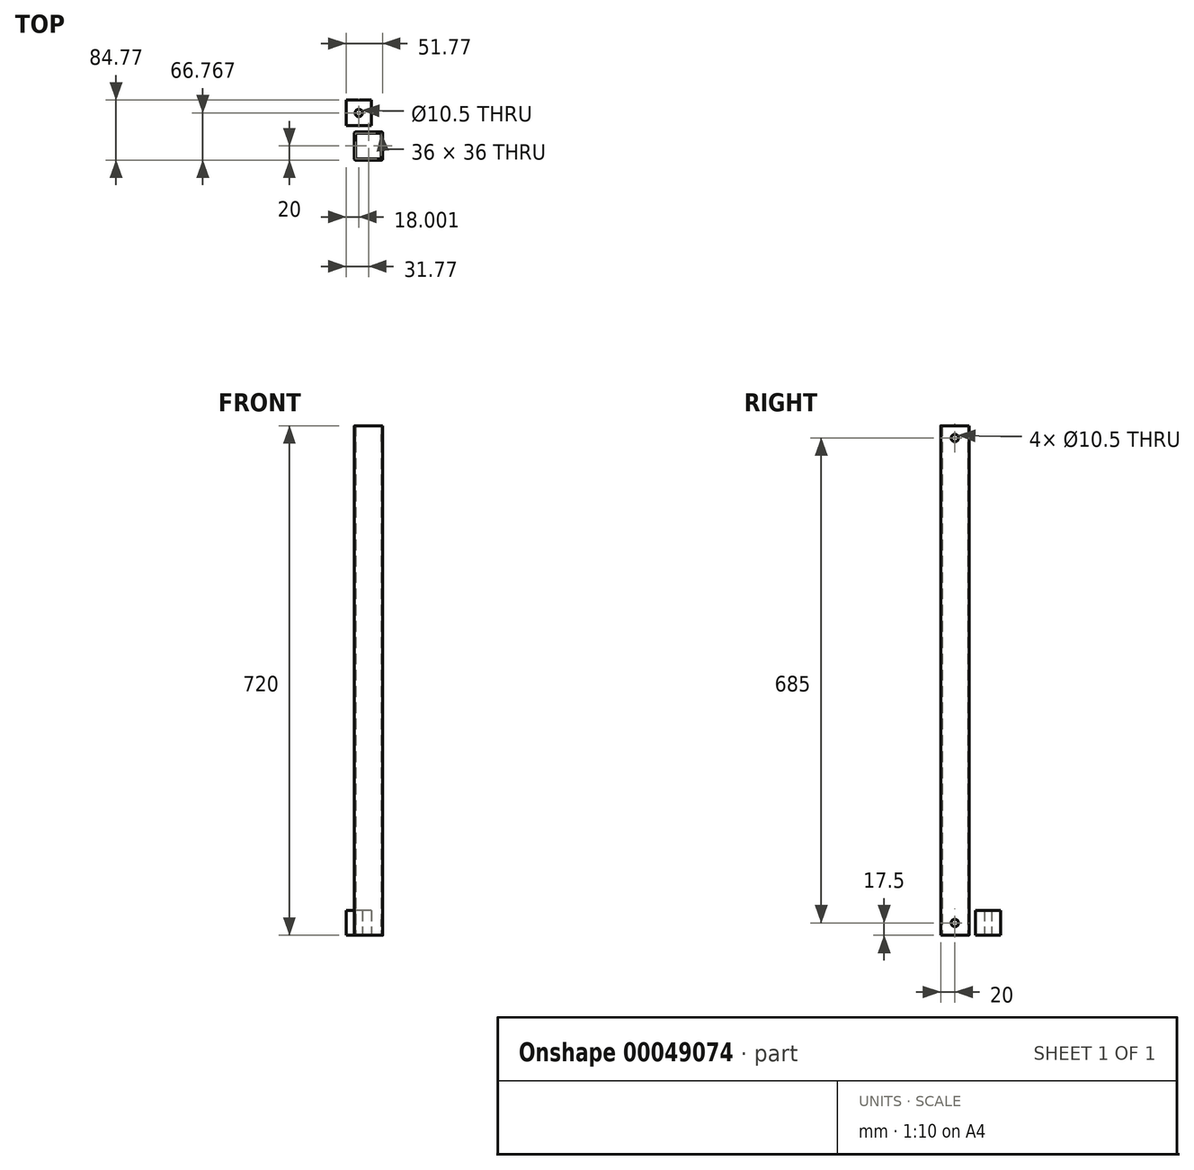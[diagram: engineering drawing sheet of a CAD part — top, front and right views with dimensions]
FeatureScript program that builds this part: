
annotation { "Feature Type Name" : "Feature", "Feature Type Description" : "" }
export const myFeature = defineFeature(function(context is Context, id is Id, definition is map)
    precondition{}
    {
        {
            var Q0;
            Q0=qCreatedBy(makeId("Top.planeOp"),FACE);
            var sketch = newSketch(context, id + "F0", { "sketchPlane" : qUnion([Q0])});
            skLineSegment(sketch, "E0.bottom", {"start": v(0, 0) * mm, "end": v(-40, 0) * mm});
            skLineSegment(sketch, "E0.top", {"start": v(0, -40) * mm, "end": v(-40, -40) * mm});
            skLineSegment(sketch, "E0.left", {"start": v(0, 0) * mm, "end": v(0, -40) * mm});
            skLineSegment(sketch, "E0.right", {"start": v(-40, 0) * mm, "end": v(-40, -40) * mm});
            skLineSegment(sketch, "E1.0", {"start": v(-2, -2) * mm, "end": v(-38, -2) * mm});
            skLineSegment(sketch, "E1.1", {"start": v(-2, -2) * mm, "end": v(-2, -38) * mm});
            skLineSegment(sketch, "E1.2", {"start": v(-2, -38) * mm, "end": v(-38, -38) * mm});
            skLineSegment(sketch, "E1.3", {"start": v(-38, -2) * mm, "end": v(-38, -38) * mm});
            skSolve(sketch);
        }
        {
            var Q0;
            Q0=qSketchRegion(id+"F0",true);
            extrude(context, id + "F1", {"entities" : qUnion([Q0]), "depth" : 720 * mm});
        }
        {
            var Q0;
            Q0=qCreatedBy(makeId("Top.planeOp"),FACE);
            var sketch = newSketch(context, id + "F2", { "sketchPlane" : qUnion([Q0])});
            skLineSegment(sketch, "E2.bottom", {"start": v(-15.77, 8.77) * mm, "end": v(-51.77, 8.77) * mm});
            skLineSegment(sketch, "E2.top", {"start": v(-15.77, 44.77) * mm, "end": v(-51.77, 44.77) * mm});
            skLineSegment(sketch, "E2.left", {"start": v(-15.77, 8.77) * mm, "end": v(-15.77, 44.77) * mm});
            skLineSegment(sketch, "E2.right", {"start": v(-51.77, 8.77) * mm, "end": v(-51.77, 44.77) * mm});
            skCircle(sketch, "E3", {"center": v(-33.77, 26.77) * mm, "radius": 5.25 * mm});
            skPoint(sketch, "E3.centerSnap0", {"position": v(-51.77, 26.77) * mm});
            skPoint(sketch, "E3.centerSnap1", {"position": v(-33.77, 8.77) * mm});
            skSolve(sketch);
        }
        {
            var Q0;
            Q0=qSketchRegion(id+"F2",true);
            extrude(context, id + "F3", {"entities" : qUnion([Q0]), "depth" : 35 * mm});
        }
        {
            var Q0;
            Q0=makeQuery(id+"F1.opExtrude","SWEPT_FACE",FACE,{"disambiguationData":[OSD([sQuery(id+"F0.wireOp",EDGE,"E0.right")])]});
            var sketch = newSketch(context, id + "F4", { "sketchPlane" : qUnion([Q0])});
            skLineSegment(sketch, "E4", {"start": v(40, 0) * mm, "end": v(0, 0) * mm});
            skLineSegment(sketch, "E5", {"start": v(40, 17.5) * mm, "end": v(0, 17.5) * mm});
            skCircle(sketch, "E6", {"center": v(20, 17.5) * mm, "radius": 5.25 * mm});
            skSolve(sketch);
        }
        {
            var Q0;
            Q0=sQuery(id+"F4.wireOp",VERTEX,"E6.center");
            var Q1;
            Q1=makeQuery(id+"F1.opExtrude","SWEPT_BODY",BODY,{"disambiguationData":[OSD([sQuery(id+"F0.wireOp",EDGE,"E0.bottom"),sQuery(id+"F0.wireOp",EDGE,"E0.top"),sQuery(id+"F0.wireOp",EDGE,"E0.left"),sQuery(id+"F0.wireOp",EDGE,"E0.right"),sQuery(id+"F0.wireOp",EDGE,"E1.0"),sQuery(id+"F0.wireOp",EDGE,"E1.1"),sQuery(id+"F0.wireOp",EDGE,"E1.2"),sQuery(id+"F0.wireOp",EDGE,"E1.3")])]});
            hole(context, id + "F5", {"style" : HoleStyle.SIMPLE, "holeDiameter" : 10.5 * mm, "endStyle" : HoleEndStyle.THROUGH, "locations" : qUnion([Q0]), "scope" : qUnion([Q1])});
        }
        {
            var Q0;
            Q0=makeQuery(id+"F1.opExtrude","SWEPT_FACE",FACE,{"disambiguationData":[OSD([sQuery(id+"F0.wireOp",EDGE,"E0.right")])]});
            var sketch = newSketch(context, id + "F6", { "sketchPlane" : qUnion([Q0])});
            skLineSegment(sketch, "E7", {"start": v(40, 720) * mm, "end": v(0, 720) * mm});
            skLineSegment(sketch, "E8", {"start": v(40, 702.5) * mm, "end": v(0, 702.5) * mm});
            skCircle(sketch, "E9", {"center": v(20, 702.5) * mm, "radius": 5.25 * mm});
            skSolve(sketch);
        }
        {
            var Q0;
            Q0=sQuery(id+"F6.wireOp",VERTEX,"E9.center");
            var Q1;
            Q1=makeQuery(id+"F1.opExtrude","SWEPT_BODY",BODY,{"disambiguationData":[OSD([sQuery(id+"F0.wireOp",EDGE,"E0.bottom"),sQuery(id+"F0.wireOp",EDGE,"E0.top"),sQuery(id+"F0.wireOp",EDGE,"E0.left"),sQuery(id+"F0.wireOp",EDGE,"E0.right"),sQuery(id+"F0.wireOp",EDGE,"E1.0"),sQuery(id+"F0.wireOp",EDGE,"E1.1"),sQuery(id+"F0.wireOp",EDGE,"E1.2"),sQuery(id+"F0.wireOp",EDGE,"E1.3")])]});
            hole(context, id + "F7", {"style" : HoleStyle.SIMPLE, "holeDiameter" : 10.5 * mm, "endStyle" : HoleEndStyle.THROUGH, "locations" : qUnion([Q0]), "scope" : qUnion([Q1])});
        }
        {
            var Q0;
            Q0=makeQuery(id+"F1.opExtrude","SWEPT_EDGE",EDGE,{"disambiguationData":[OSD([sQuery(id+"F0.wireOp",EDGE,"E0.top"),sQuery(id+"F0.wireOp",EDGE,"E0.left")])]});
            var Q1;
            Q1=makeQuery(id+"F1.opExtrude","SWEPT_EDGE",EDGE,{"disambiguationData":[OSD([sQuery(id+"F0.wireOp",EDGE,"E0.top"),sQuery(id+"F0.wireOp",EDGE,"E0.right")])]});
            var Q2;
            Q2=makeQuery(id+"F1.opExtrude","SWEPT_EDGE",EDGE,{"disambiguationData":[OSD([sQuery(id+"F0.wireOp",EDGE,"E0.bottom"),sQuery(id+"F0.wireOp",EDGE,"E0.left")])]});
            var Q3;
            Q3=makeQuery(id+"F1.opExtrude","SWEPT_EDGE",EDGE,{"disambiguationData":[OSD([sQuery(id+"F0.wireOp",EDGE,"E0.bottom"),sQuery(id+"F0.wireOp",EDGE,"E0.right")])]});
            fillet(context, id + "F8", {"entities" : qUnion([Q0, Q1, Q2, Q3]), "radius" : 2 * mm, "tangentPropagation" : true, "allowEdgeOverflow" : false});
        }
    });
